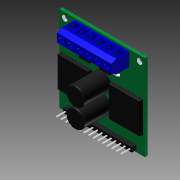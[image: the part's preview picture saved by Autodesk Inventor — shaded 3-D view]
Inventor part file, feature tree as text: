
AUTODESK INVENTOR PART (.ipt)
format: ipt  version: 2012 (Build 160160000, 160)  size: 527,360 bytes
history: native  units: in
note: dims shown in document units (in); Inventor stores cm internally (conversion verified against a paired STEP export)
features: extrude x11, chamfer x5, fillet x3, sketch x2
ambient origin geometry x8: Origin, YZ Plane, XZ Plane, XY Plane, X Axis, Y Axis, Z Axis, Center Point
bodies: Solid1 (feature_tree)
feature tree (21):
  sketch  "Sketch1"  dims[d0=1.86in d1=1.86in]
  extrude  "Extrusion1"  Depth=1.86in
  extrude  "Extrusion2"  Depth=0.1181in
  extrude  "Extrusion3"  Depth=0.1181in
  extrude  "Extrusion4"  Depth=0.1181in
  extrude  "Extrusion5"  Depth=0.1181in
  extrude  "Extrusion6"  Depth=0.1181in
  fillet  "Fillet1"  Radius=1.1811in
  fillet  "Fillet2"  Radius=0.3937in
  chamfer  "Chamfer1"  Distance=0.3937in
  chamfer  "Chamfer2"  Distance=0.3394in
  extrude  "Extrusion7"  Depth=0.0394in
  extrude  "Extrusion8"  Depth=0.2953in
  extrude  "Extrusion9"  Depth=1.4843in
  fillet  "Fillet3"  Radius=0.188in
  extrude  "Extrusion10"  Depth=0.6693in
  extrude  "Extrusion11"  Depth=0.6693in
  chamfer  "Chamfer3"  Distance=0.6693in
  chamfer  "Chamfer4"  Distance=0.6693in
  chamfer  "Chamfer5"  Distance=0.7874in
  sketch  "Sketch2"  dims[d2=0.1181in d3=0.1181in d4=0.1181in d5=0.1181in d6=0.1181in d7=0.1181in d8=1.1811in d9=0.3937in d10=0.3937in d11=0.3394in d12=0.0394in d13=0.2953in d14=1.4843in d15=0.188in d16=0.6693in d17=0.6693in d18=0.6693in d19=0.6693in d20=0.7874in d21=0.7874in d23=0.0197in d24=0.0197in d25=0.0197in d26=0.0197in d27=0.0197in d28=0.0197in d29=0.0197in d30=0.0197in d31=0.0197in d32=0.0197in d33=0.0197in d34=0.0197in d35=0.0197in d36=0.0197in d37=0.0197in d38=0.0197in d39=0.0197in d40=0.0197in d41=0.0197in d42=0.0197in d43=0.0197in d44=0.0197in d45=0.0197in d46=0.0197in d47=0.0197in d48=0.0197in d49=0.0197in d50=0.0197in d51=0.0197in d52=0.0197in d53=0.0325in d54=0.1in d55=0.1in d56=0.1in d57=0.1in d58=0.1in d59=0.1in d60=0.1in d61=0.1in d62=0.1in d63=0.1in d64=0.1in d65=0.1in d66=0.1in d67=0.0999in d68=0.0394in d69=0.0394in d70=0.3937in d71=0.3937in d72=0.1181in d73=0.1181in d74=0.1181in d75=0.1181in d76=0.1181in d77=0.1181in d78=0.041in d79=0.041in d80=0.041in d81=0.041in d82=0.041in d83=0.041in d84=0.0984in d85=0.0in d86=0.2953in d87=0.0in d88=0.0984in d89=0.0395in d90=0.0395in d91=0.0395in d92=0.0395in d93=0.0395in d94=0.0395in d95=0.0395in d96=0.0395in d97=0.0395in d98=0.0395in d99=0.0395in d100=0.0395in d101=0.0395in d102=0.0395in d103=0.0395in d104=0.2643in d105=0.0787in d106=0.0in d107=0.3937in d108=0.0in d109=0.2953in d110=0.0in d111=0.5906in d112=0.0in d113=0.02in d114=0.01in d115=0.07in d116=0.125in d117=60.0deg d118=0.04in d119=0.125in d120=0.481in d121=0.0394in d122=0.0394in d123=0.0394in d124=0.0394in d125=0.0394in d126=0.1575in d127=0.1575in d128=0.1575in d129=0.1575in d130=0.1575in d131=0.1575in d132=0.1969in d133=0.1969in d134=0.1969in d135=0.1969in d136=0.1969in d137=0.1969in d138=0.0435in d139=0.0435in d140=0.0435in d141=0.0435in d142=0.0435in d143=0.0435in d144=0.0197in d145=0.2362in d146=0.0in d147=0.063in d148=0.0in d149=0.2362in d150=0.2362in d151=0.2362in d152=0.2362in d153=0.5118in d154=0.6693in d155=0.0394in d156=0.0394in d157=0.0984in d158=-0.0in d159=0.01in d160=0.09in d161=0.09in d162=0.13in d163=0.13in d164=0.04in d165=0.04in d166=0.02in d167=0.02in d168=0.04in d169=0.13in d170=0.13in d171=0.04in d172=0.04in d173=0.04in d174=0.02in d175=0.02in d176=0.0394in d177=0.0in d178=0.0197in d179=0.0in d180=0.039in d181=0.125in d182=45.0deg d183=0.01in d184=0.125in d185=45.0deg d186=0.005in d187=0.125in d188=45.0deg]
